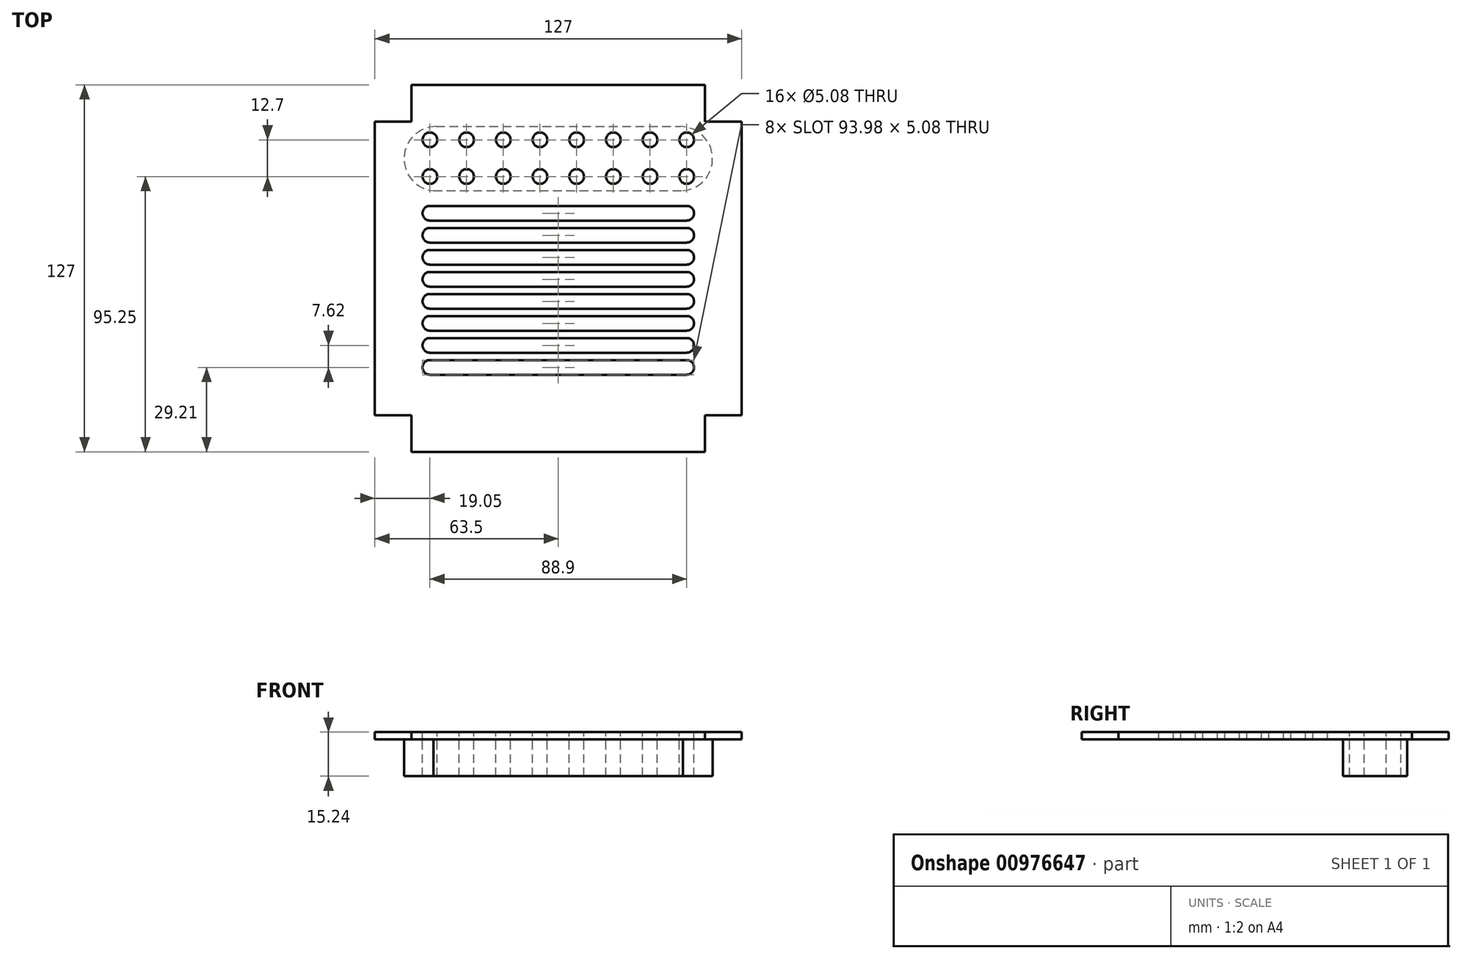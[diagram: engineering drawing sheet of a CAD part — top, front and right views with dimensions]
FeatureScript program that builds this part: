
annotation { "Feature Type Name" : "Feature", "Feature Type Description" : "" }
export const myFeature = defineFeature(function(context is Context, id is Id, definition is map)
    precondition{}
    {
        {
            var Q0;
            Q0=qCreatedBy(makeId("Top.planeOp"),FACE);
            var sketch = newSketch(context, id + "F0", { "sketchPlane" : qUnion([Q0])});
            skLineSegment(sketch, "E0", {"start": v(0, 63.5) * mm, "end": v(50.8, 63.5) * mm});
            skLineSegment(sketch, "E1", {"start": v(50.8, 63.5) * mm, "end": v(50.8, 50.8) * mm});
            skLineSegment(sketch, "E2", {"start": v(50.8, 50.8) * mm, "end": v(63.5, 50.8) * mm});
            skLineSegment(sketch, "E3", {"start": v(63.5, 50.8) * mm, "end": v(63.5, 0) * mm});
            skLineSegment(sketch, "E4.MirrorCS", {"start": v(0, -63.5) * mm, "end": v(50.8, -63.5) * mm});
            skLineSegment(sketch, "E5.MirrorCS", {"start": v(50.8, -63.5) * mm, "end": v(50.8, -50.8) * mm});
            skLineSegment(sketch, "E6.MirrorCS", {"start": v(50.8, -50.8) * mm, "end": v(63.5, -50.8) * mm});
            skLineSegment(sketch, "E7.MirrorCS", {"start": v(63.5, -50.8) * mm, "end": v(63.5, 0) * mm});
            skLineSegment(sketch, "E8.MirrorCS", {"start": v(0, 63.5) * mm, "end": v(-50.8, 63.5) * mm});
            skLineSegment(sketch, "E9.MirrorCS", {"start": v(-50.8, 63.5) * mm, "end": v(-50.8, 50.8) * mm});
            skLineSegment(sketch, "E10.MirrorCS", {"start": v(-50.8, 50.8) * mm, "end": v(-63.5, 50.8) * mm});
            skLineSegment(sketch, "E11.MirrorCS", {"start": v(-63.5, 50.8) * mm, "end": v(-63.5, 0) * mm});
            skLineSegment(sketch, "E12.MirrorCS", {"start": v(-63.5, -50.8) * mm, "end": v(-63.5, 0) * mm});
            skLineSegment(sketch, "E13.MirrorCS", {"start": v(-50.8, -50.8) * mm, "end": v(-63.5, -50.8) * mm});
            skLineSegment(sketch, "E14.MirrorCS", {"start": v(-50.8, -63.5) * mm, "end": v(-50.8, -50.8) * mm});
            skLineSegment(sketch, "E15.MirrorCS", {"start": v(0, -63.5) * mm, "end": v(-50.8, -63.5) * mm});
            skSolve(sketch);
        }
        {
            var Q0;
            Q0 = qSketchRegion(id + "F0", true);
            extrude(context, id + "F1", {"entities" : qUnion([Q0]), "depth" : 2.54 * mm, "offsetDistance" : 25.4 * mm});
        }
        {
            var Q0;
            Q0=makeQuery(id+"F1.opExtrude","CAP_FACE",FACE,{"disambiguationData":[OSD([sQuery(id+"F0.wireOp",EDGE,"E0"),sQuery(id+"F0.wireOp",EDGE,"E1"),sQuery(id+"F0.wireOp",EDGE,"E2"),sQuery(id+"F0.wireOp",EDGE,"E3"),sQuery(id+"F0.wireOp",EDGE,"E4.MirrorCS"),sQuery(id+"F0.wireOp",EDGE,"E5.MirrorCS"),sQuery(id+"F0.wireOp",EDGE,"E6.MirrorCS"),sQuery(id+"F0.wireOp",EDGE,"E7.MirrorCS"),sQuery(id+"F0.wireOp",EDGE,"E8.MirrorCS"),sQuery(id+"F0.wireOp",EDGE,"E9.MirrorCS"),sQuery(id+"F0.wireOp",EDGE,"E10.MirrorCS"),sQuery(id+"F0.wireOp",EDGE,"E11.MirrorCS"),sQuery(id+"F0.wireOp",EDGE,"E12.MirrorCS"),sQuery(id+"F0.wireOp",EDGE,"E13.MirrorCS"),sQuery(id+"F0.wireOp",EDGE,"E14.MirrorCS"),sQuery(id+"F0.wireOp",EDGE,"E15.MirrorCS")])],"isStart":true});
            var sketch = newSketch(context, id + "F2", { "sketchPlane" : qUnion([Q0])});
            skLineSegment(sketch, "E16.bottom", {"start": v(-43.21, -26.82) * mm, "end": v(43.21, -26.82) * mm});
            skLineSegment(sketch, "E16.top", {"start": v(-42.26, -49.03) * mm, "end": v(42.26, -49.03) * mm});
            skArc(sketch, "E17", {"start": v(-43.21, -26.82) * mm, "mid": v(-53.38, -38.38) * mm, "end": v(-42.26, -49.03) * mm});
            skArc(sketch, "E18", {"start": v(42.26, -49.03) * mm, "mid": v(53.38, -38.38) * mm, "end": v(43.21, -26.82) * mm});
            skSolve(sketch);
        }
        {
            var Q0;
            Q0 = qSketchRegion(id + "F2", true);
            var Q1;
            Q1 = qSketchRegion(id + "F4", true);
            extrude(context, id + "F3", {"entities" : qUnion([Q0, Q1]), "operationType" : NewBodyOperationType.ADD, "depth" : 12.7 * mm, "offsetDistance" : 25.4 * mm});
        }
        {
            var Q0;
            Q0=makeQuery(id+"F1.opExtrude","CAP_FACE",FACE,{"disambiguationData":[OSD([sQuery(id+"F0.wireOp",EDGE,"E0"),sQuery(id+"F0.wireOp",EDGE,"E1"),sQuery(id+"F0.wireOp",EDGE,"E2"),sQuery(id+"F0.wireOp",EDGE,"E3"),sQuery(id+"F0.wireOp",EDGE,"E4.MirrorCS"),sQuery(id+"F0.wireOp",EDGE,"E5.MirrorCS"),sQuery(id+"F0.wireOp",EDGE,"E6.MirrorCS"),sQuery(id+"F0.wireOp",EDGE,"E7.MirrorCS"),sQuery(id+"F0.wireOp",EDGE,"E8.MirrorCS"),sQuery(id+"F0.wireOp",EDGE,"E9.MirrorCS"),sQuery(id+"F0.wireOp",EDGE,"E10.MirrorCS"),sQuery(id+"F0.wireOp",EDGE,"E11.MirrorCS"),sQuery(id+"F0.wireOp",EDGE,"E12.MirrorCS"),sQuery(id+"F0.wireOp",EDGE,"E13.MirrorCS"),sQuery(id+"F0.wireOp",EDGE,"E14.MirrorCS"),sQuery(id+"F0.wireOp",EDGE,"E15.MirrorCS")])],"isStart":false});
            var sketch = newSketch(context, id + "F4", { "sketchPlane" : qUnion([Q0])});
            skCircle(sketch, "E19", {"center": v(-44.45, 44.45) * mm, "radius": 2.54 * mm});
            skCircle(sketch, "E20.0.1.0", {"center": v(-44.45, 31.75) * mm, "radius": 2.54 * mm});
            skCircle(sketch, "E20.1.0.0", {"center": v(-31.75, 44.45) * mm, "radius": 2.54 * mm});
            skCircle(sketch, "E20.1.1.0", {"center": v(-31.75, 31.75) * mm, "radius": 2.54 * mm});
            skCircle(sketch, "E20.2.0.0", {"center": v(-19.05, 44.45) * mm, "radius": 2.54 * mm});
            skCircle(sketch, "E20.2.1.0", {"center": v(-19.05, 31.75) * mm, "radius": 2.54 * mm});
            skCircle(sketch, "E20.3.0.0", {"center": v(-6.35, 44.45) * mm, "radius": 2.54 * mm});
            skCircle(sketch, "E20.3.1.0", {"center": v(-6.35, 31.75) * mm, "radius": 2.54 * mm});
            skCircle(sketch, "E20.4.0.0", {"center": v(6.35, 44.45) * mm, "radius": 2.54 * mm});
            skCircle(sketch, "E20.4.1.0", {"center": v(6.35, 31.75) * mm, "radius": 2.54 * mm});
            skCircle(sketch, "E20.5.0.0", {"center": v(19.05, 44.45) * mm, "radius": 2.54 * mm});
            skCircle(sketch, "E20.5.1.0", {"center": v(19.05, 31.75) * mm, "radius": 2.54 * mm});
            skCircle(sketch, "E20.6.0.0", {"center": v(31.75, 44.45) * mm, "radius": 2.54 * mm});
            skCircle(sketch, "E20.6.1.0", {"center": v(31.75, 31.75) * mm, "radius": 2.54 * mm});
            skCircle(sketch, "E20.7.0.0", {"center": v(44.45, 44.45) * mm, "radius": 2.54 * mm});
            skCircle(sketch, "E20.7.1.0", {"center": v(44.45, 31.75) * mm, "radius": 2.54 * mm});
            skLineSegment(sketch, "E20.direction1", {"start": v(-44.45, 44.45) * mm, "end": v(-31.75, 44.45) * mm, "construction": true});
            skLineSegment(sketch, "E20.direction2", {"start": v(-44.45, 44.45) * mm, "end": v(-44.45, 31.75) * mm, "construction": true});
            skLineSegment(sketch, "E21", {"start": v(-44.45, 21.59) * mm, "end": v(44.45, 21.59) * mm});
            skLineSegment(sketch, "E22.0.1.0", {"start": v(-44.45, 16.5) * mm, "end": v(44.45, 16.5) * mm});
            skLineSegment(sketch, "E22.direction1", {"start": v(-44.45, 21.59) * mm, "end": v(-19.05, 21.59) * mm, "construction": true});
            skLineSegment(sketch, "E22.direction2", {"start": v(-44.45, 21.59) * mm, "end": v(-44.45, 16.5) * mm, "construction": true});
            skArc(sketch, "E23", {"start": v(-44.45, 21.59) * mm, "mid": v(-46.99, 19.05) * mm, "end": v(-44.45, 16.5) * mm});
            skArc(sketch, "E24", {"start": v(44.45, 16.5) * mm, "mid": v(47, 19.05) * mm, "end": v(44.45, 21.59) * mm});
            skLineSegment(sketch, "E25.0.1.0", {"start": v(-44.45, 13.97) * mm, "end": v(44.45, 13.97) * mm});
            skArc(sketch, "E25.0.1.1", {"start": v(-44.45, 13.97) * mm, "mid": v(-46.99, 11.43) * mm, "end": v(-44.45, 8.89) * mm});
            skLineSegment(sketch, "E25.0.1.2", {"start": v(-44.45, 8.89) * mm, "end": v(44.45, 8.89) * mm});
            skArc(sketch, "E25.0.1.3", {"start": v(44.45, 8.89) * mm, "mid": v(47, 11.43) * mm, "end": v(44.45, 13.97) * mm});
            skLineSegment(sketch, "E25.direction1", {"start": v(-44.45, 21.59) * mm, "end": v(-69.85, 21.59) * mm, "construction": true});
            skLineSegment(sketch, "E25.direction2", {"start": v(-44.45, 21.59) * mm, "end": v(-44.45, 13.97) * mm, "construction": true});
            skLineSegment(sketch, "E26.0.1.0", {"start": v(-44.45, 6.35) * mm, "end": v(44.45, 6.35) * mm});
            skArc(sketch, "E26.0.1.1", {"start": v(44.45, 1.27) * mm, "mid": v(47, 3.8) * mm, "end": v(44.45, 6.35) * mm});
            skLineSegment(sketch, "E26.0.1.2", {"start": v(-44.45, 1.27) * mm, "end": v(44.45, 1.27) * mm});
            skArc(sketch, "E26.0.1.3", {"start": v(-44.45, 6.35) * mm, "mid": v(-46.99, 3.8) * mm, "end": v(-44.45, 1.27) * mm});
            skLineSegment(sketch, "E26.0.1.4", {"start": v(-44.45, -1.27) * mm, "end": v(44.45, -1.27) * mm});
            skArc(sketch, "E26.0.1.5", {"start": v(-44.45, -1.27) * mm, "mid": v(-46.99, -3.81) * mm, "end": v(-44.45, -6.35) * mm});
            skLineSegment(sketch, "E26.0.1.6", {"start": v(-44.45, -6.35) * mm, "end": v(44.45, -6.35) * mm});
            skArc(sketch, "E26.0.1.7", {"start": v(44.45, -6.35) * mm, "mid": v(47, -3.81) * mm, "end": v(44.45, -1.27) * mm});
            skLineSegment(sketch, "E26.0.2.0", {"start": v(-44.45, -8.9) * mm, "end": v(44.45, -8.9) * mm});
            skArc(sketch, "E26.0.2.1", {"start": v(44.45, -13.97) * mm, "mid": v(47, -11.43) * mm, "end": v(44.45, -8.89) * mm});
            skLineSegment(sketch, "E26.0.2.2", {"start": v(-44.45, -13.97) * mm, "end": v(44.45, -13.97) * mm});
            skArc(sketch, "E26.0.2.3", {"start": v(-44.45, -8.9) * mm, "mid": v(-46.99, -11.43) * mm, "end": v(-44.45, -13.97) * mm});
            skLineSegment(sketch, "E26.0.2.4", {"start": v(-44.45, -16.51) * mm, "end": v(44.45, -16.51) * mm});
            skArc(sketch, "E26.0.2.5", {"start": v(-44.45, -16.51) * mm, "mid": v(-46.99, -19.05) * mm, "end": v(-44.45, -21.6) * mm});
            skLineSegment(sketch, "E26.0.2.6", {"start": v(-44.45, -21.6) * mm, "end": v(44.45, -21.6) * mm});
            skArc(sketch, "E26.0.2.7", {"start": v(44.45, -21.6) * mm, "mid": v(47, -19.05) * mm, "end": v(44.45, -16.51) * mm});
            skLineSegment(sketch, "E26.0.3.0", {"start": v(-44.45, -24.13) * mm, "end": v(44.45, -24.13) * mm});
            skArc(sketch, "E26.0.3.1", {"start": v(44.45, -29.21) * mm, "mid": v(47, -26.67) * mm, "end": v(44.45, -24.13) * mm});
            skLineSegment(sketch, "E26.0.3.2", {"start": v(-44.45, -29.21) * mm, "end": v(44.45, -29.21) * mm});
            skArc(sketch, "E26.0.3.3", {"start": v(-44.45, -24.13) * mm, "mid": v(-46.99, -26.67) * mm, "end": v(-44.45, -29.21) * mm});
            skLineSegment(sketch, "E26.0.3.4", {"start": v(-44.45, -31.75) * mm, "end": v(44.45, -31.75) * mm});
            skArc(sketch, "E26.0.3.5", {"start": v(-44.45, -31.75) * mm, "mid": v(-46.99, -34.3) * mm, "end": v(-44.45, -36.83) * mm});
            skLineSegment(sketch, "E26.0.3.6", {"start": v(-44.45, -36.83) * mm, "end": v(44.45, -36.83) * mm});
            skArc(sketch, "E26.0.3.7", {"start": v(44.45, -36.83) * mm, "mid": v(47, -34.3) * mm, "end": v(44.45, -31.75) * mm});
            skLineSegment(sketch, "E26.direction1", {"start": v(-44.45, 8.89) * mm, "end": v(-19.05, 8.89) * mm, "construction": true});
            skLineSegment(sketch, "E26.direction2", {"start": v(-44.45, 8.89) * mm, "end": v(-44.45, -6.35) * mm, "construction": true});
            skSolve(sketch);
        }
        {
            var Q0;
            Q0 = qSketchRegion(id + "F4", true);
            extrude(context, id + "F5", {"entities" : qUnion([Q0]), "operationType" : NewBodyOperationType.REMOVE, "oppositeDirection" : true, "depth" : 25.4 * mm, "offsetDistance" : 25.4 * mm});
        }
    });
